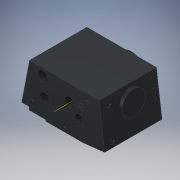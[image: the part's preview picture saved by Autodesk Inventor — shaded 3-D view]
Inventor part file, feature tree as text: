
AUTODESK INVENTOR PART (.ipt)
format: ipt  version: 2018 (Build 220112000, 112)  size: 362,496 bytes
history: native  units: in
note: dims shown in document units (in); Inventor stores cm internally (conversion verified against a paired STEP export)
features: extrude x23, sketch x21, fillet x2, thread x2, plane x2, hole x1, other x1
ambient origin geometry x8: Origin, YZ Plane, XZ Plane, XY Plane, X Axis, Y Axis, Z Axis, Center Point
bodies: Solid1 (feature_tree)
feature tree (52):
  extrude  "Extrusion1"  Depth=10.4921in
  sketch  "Sketch3"  dims[d7=10.0in d8=0.5669in]
  extrude  "Extrusion2"  Depth=0.5669in
  extrude  "Extrusion3"  Depth=0.694in
  extrude  "Extrusion4"  Depth=0.7087in
  extrude  "Extrusion5"  Depth=0.0787in
  extrude  "Extrusion6"  Depth=13.4646in TaperAngle=0.0deg
  fillet  "Fillet1"  Radius=5.5118in
  fillet  "Fillet2"  Radius=6.2992in
  extrude  "Extrusion7"  Depth=2.7559in
  thread  "Thread1"  [1 undecoded]
  extrude  "Extrusion8"  Depth=1.1811in
  plane  "Work Plane3"
  extrude  "Extrusion10"  Depth=1.7717in
  extrude  "Extrusion11"  Depth=1.2106in
  extrude  "Extrusion12"  Depth=2.3622in TaperAngle=0.0deg
  extrude  "Extrusion13"  Depth=0.748in
  extrude  "Extrusion14"  Depth=1.0236in TaperAngle=0.0deg
  hole  "Hole1"  [1 undecoded]
  extrude  "Extrusion15"  Depth=1.378in
  extrude  "Extrusion16"  Depth=0.315in
  extrude  "Extrusion17"  Depth=0.0787in
  thread  "Thread2"  [1 undecoded]
  plane  "Work Plane2"
  extrude  "Extrusion18"  Depth=1.1811in TaperAngle=0.0deg
  extrude  "Extrusion19"  Depth=0.3937in
  extrude  "Extrusion20"  Depth=0.3937in TaperAngle=0.0deg
  sketch  "Sketch25"  dims[d88=45.0deg d91=0.3937in d92=0.0in]
  extrude  "Extrusion21"  Depth=1.1811in
  extrude  "Extrusion22"  Depth=0.3937in TaperAngle=0.0deg
  extrude  "Extrusion23"  Depth=0.1969in
  extrude  "Extrusion24"  Depth=0.1969in
  sketch  "Sketch1"  dims[d0=8.6614in d1=10.4921in]
  sketch  "Sketch4"  dims[d9=9.6457in d10=0.694in]
  sketch  "Sketch5"  dims[d11=1.7717in d12=0.7087in]
  sketch  "Sketch6"  dims[d14=16.3386in d15=0.0787in]
  sketch  "Sketch7"  dims[d16=0.0787in d17=13.4646in d18=0.0in d22=5.5118in d26=6.2992in]
  sketch  "Sketch8"  dims[d27=2.7559in d28=3.6024in d29=2.7559in]
  sketch  "Sketch10"  dims[d30=0.3937in d31=0.0in d34=1.1811in]
  sketch  "Sketch12"  dims[d37=1.7717in d38=2.0079in]
  sketch  "Sketch13"  dims[d39=1.2402in d42=1.2106in]
  sketch  "Sketch14"  dims[d43=1.8799in d44=2.3622in d45=0.0in]
  sketch  "Sketch16"  dims[d49=6.3386in d50=0.748in]
  sketch  "Sketch17"  dims[d52=7.4213in d53=1.0236in d54=0.0in]
  sketch  "Sketch19"  dims[d55=2.2835in d56=1.0236in d57=0.0in]
  sketch  "Sketch20"  dims[d69=0.7874in d70=1.378in]
  sketch  "Sketch21"  dims[d72=0.3937in d73=0.315in]
  other  "Work Axis1"
  sketch  "Sketch22"  dims[d75=0.2362in d76=0.0in d77=0.0787in d78=0.0787in]
  sketch  "Sketch23"  dims[d82=0.7874in d83=1.1811in d84=0.0in]
  sketch  "Sketch24"  dims[d85=0.3937in d86=0.0in d87=3.0118in]
  sketch  "Sketch26"  dims[d97=1.9685in d98=0.0in d103=1.1811in d105=0.3937in d106=0.0in d107=5.9055in d108=5.9646in d109=90.0deg d110=2.7559in d111=7.4803in d112=90.0deg d113=0.3937in d114=0.0in d116=0.3937in d117=0.0in d118=2.9528in d120=3.2283in d121=1.1811in d122=0.1969in d123=0.0in d124=0.2559in d125=0.1181in d126=0.2362in d127=0.2559in d128=0.0787in d129=90.0deg d130=0.1969in d131=0.0in d132=6.6929in d133=90.0deg d134=1.7323in d135=2.4409in d136=0.7874in d137=0.0in d138=5.9055in d139=5.9646in d140=90.0deg d141=2.1654in d142=2.7559in d143=0.0in d144=0.9843in d145=1.3386in d146=0.7874in d147=0.7874in d148=0.0in d149=0.3937in d150=0.0in d151=0.0in d152=1.2992in d153=0.0in d154=17.3258in d155=0.0in d156=0.4331in d157=0.0in d160=0.1969in d163=0.1969in d164=0.1969in d165=0.5512in d166=0.0in d167=0.5512in d168=0.0in d169=0.5512in d170=0.0in d171=0.0394in d172=0.0in]
note: 3 required parameter values undecoded (feature->parameter linkage not recoverable at this tier; creation-order binding heuristic only, values carry confidence <= 0.55)
